# Revit family: L-E-713-DN_RFA
name_source: partatom
category: Aparatos sanitarios
units: mm (PartAtom-declared; Revit-internal decimal feet)

## family parameters
Activar corte en vistas = No
Compartido = Sí
Corte con vacíos al cargar = No
Cota de conector redondo = Usar diámetro
Mantener orientación de anotación = No
Número OmniClass = 23.45.05.14.99
Punto de cálculo de habitación = Sí
Se basa en plano de trabajo = Sí
Siempre vertical = Sí
Tipo de pieza = Normal
Título OmniClass = Other Sanitary Washing Plumbing Fixtures

## types (1)
- L-E-713
    Altura = 7"
    Ancho = 4"
    Comentarios de tipo = Monomando Regadera Máxima
    Descripción = Monomando para regadera, tina o regadera de
mano, con desviador con cartucho cerámico
de 35 mm.
Incluye una caja de instalación rápida con nivel de
profundidad, nivel de burbuja para nivelar en el
plano horizontal y vertical, conexiones hembra
roscadas para eliminar fugas de conexión.
En caso de fuga el agua se encapsula en el
interior de la caja de instalación y no se expande
al muro, la caja se puede instalar de dorso contra
dorso.
La forma cuadrada de la caja de instalación
permite cortes en ángulo recto.
    Duna = Duna
    Elevación por defecto = 0"
    Fabricante = HELVEX S.A. DE C.V.
    Garantía = El producto HELVEX está garantizado como
libre de defectos en materiales, mano de obra y
procesos de fabricación.
El producto HELVEX está garantizado,en lo que
se refiere a los acabados, por 10 años para los
acabados Cromo y Duravex, y por 2 años en
acabados diferentes al Cromo y Duravex.
Las piezas que sufren desgaste natural en el
producto están garantizadas para uso
residencial por 5 años, y para uso comercial por
3 años.
La vigencia de la garantía inicia a partir de la
fecha de entrega del producto al consumidor
indicada en la Póliza de Garantía.
    Imagen de tipo = <Ninguno>
    Instalación = Conxión interna ½" - 14 NPT
    Modelo = L-E-713
    Operación = Para abrir el flujo de agua levante la palanca
y para cerrar baje la palanca. Para ajustar
la temperatura del agua, gire a la izquierda para
caliente y gire a la derecha para fría.
    Presión máxima de trabajo = 85.3 psi
    Presión mínima de trabajo = 14.2 psi
    Profundidad = 5"
    Titanium = Titanium

## geometry (parser evidence)
native form markers: Sweep x3
no freeform markers — native parametric forms only
